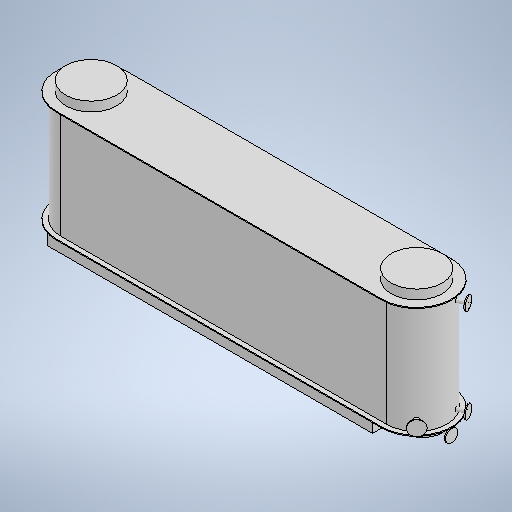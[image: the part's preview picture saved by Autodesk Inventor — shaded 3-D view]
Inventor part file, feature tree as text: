
AUTODESK INVENTOR PART (.ipt)
format: ipt  version: 2025.3 (Build 293356030, 356C)  size: 350,720 bytes
history: native  units: mm
features: sketch x13, extrude x12, projected_geometry x8, plane x3
ambient origin geometry x8: Origin, YZ Plane, XZ Plane, XY Plane, X Axis, Y Axis, Z Axis, Center Point
bodies: Solid1 (feature_tree)
feature tree (36):
  extrude  "Extrusion1"  Depth=650.0mm
  extrude  "Extrusion2"  Depth=50.0mm
  extrude  "Extrusion3"  Depth=50.0mm
  extrude  "Extrusion4"  Depth=10.0mm
  plane  "Work Plane1"
  extrude  "Extrusion5"  Depth=100.0mm
  extrude  "Extrusion6"  Depth=375.0mm TaperAngle=0.0deg
  sketch  "Sketch7"  dims[d18=135.0mm d19=10.0mm d20=0.0mm]
  plane  "Work Plane2"
  plane  "Work Plane3"
  extrude  "Extrusion7"  Depth=10.0mm TaperAngle=0.0deg
  extrude  "Extrusion8"  TaperAngle=45.0deg  [1 undecoded]
  extrude  "Extrusion9"  Depth=50.0mm TaperAngle=0.0deg
  extrude  "Extrusion10"  Depth=50.0mm TaperAngle=0.0deg
  extrude  "Extrusion11"  Depth=10.0mm TaperAngle=0.0deg
  extrude  "Extrusion12"  Depth=135.0mm
  sketch  "Sketch1"  dims[d0=3500.0mm d1=650.0mm]
  sketch  "Sketch2"  dims[d2=1200.0mm d3=0.0mm d4=50.0mm]
  projected_geometry  "Projected Loop1"
  sketch  "Sketch3"  dims[d5=10.0mm d6=0.0mm d7=50.0mm]
  projected_geometry  "Projected Loop2"
  sketch  "Sketch4"  dims[d8=10.0mm d9=0.0mm d10=400.0mm]
  sketch  "Sketch5"  dims[d11=100.0mm d12=0.0mm d13=40.0mm]
  projected_geometry  "Projected Loop3"
  projected_geometry  "Projected Loop4"
  sketch  "Sketch6"  dims[d14=30.0mm d15=375.0mm d16=0.0mm]
  projected_geometry  "Projected Loop5"
  projected_geometry  "Projected Loop6"
  sketch  "Sketch8"  dims[d21=22.5deg d23=45.0deg]
  projected_geometry  "Projected Loop7"
  sketch  "Sketch9"  dims[d24=40.0mm d27=50.0mm d28=100.0mm d29=0.0mm d30=0.0mm]
  projected_geometry  "Projected Loop8"
  sketch  "Sketch10"  dims[d31=63.0mm d33=50.0mm d34=100.0mm d35=0.0mm d36=0.0mm]
  sketch  "Sketch13"  dims[d37=160.0mm d38=10.0mm d39=0.0mm]
  sketch  "Sketch14"  dims[d40=137.5mm d44=135.0mm]
  sketch  "Sketch15"  dims[d45=135.0mm d46=10.0mm d47=0.0mm d48=550.0mm d49=550.0mm d50=100.0mm d51=0.0mm d52=100.0mm d53=550.0mm d55=200.0mm d56=0.0mm d58=1950.0mm d59=70.0mm d60=1550.0mm]
note: 1 required parameter value undecoded (feature->parameter linkage not recoverable at this tier; creation-order binding heuristic only, values carry confidence <= 0.55)
